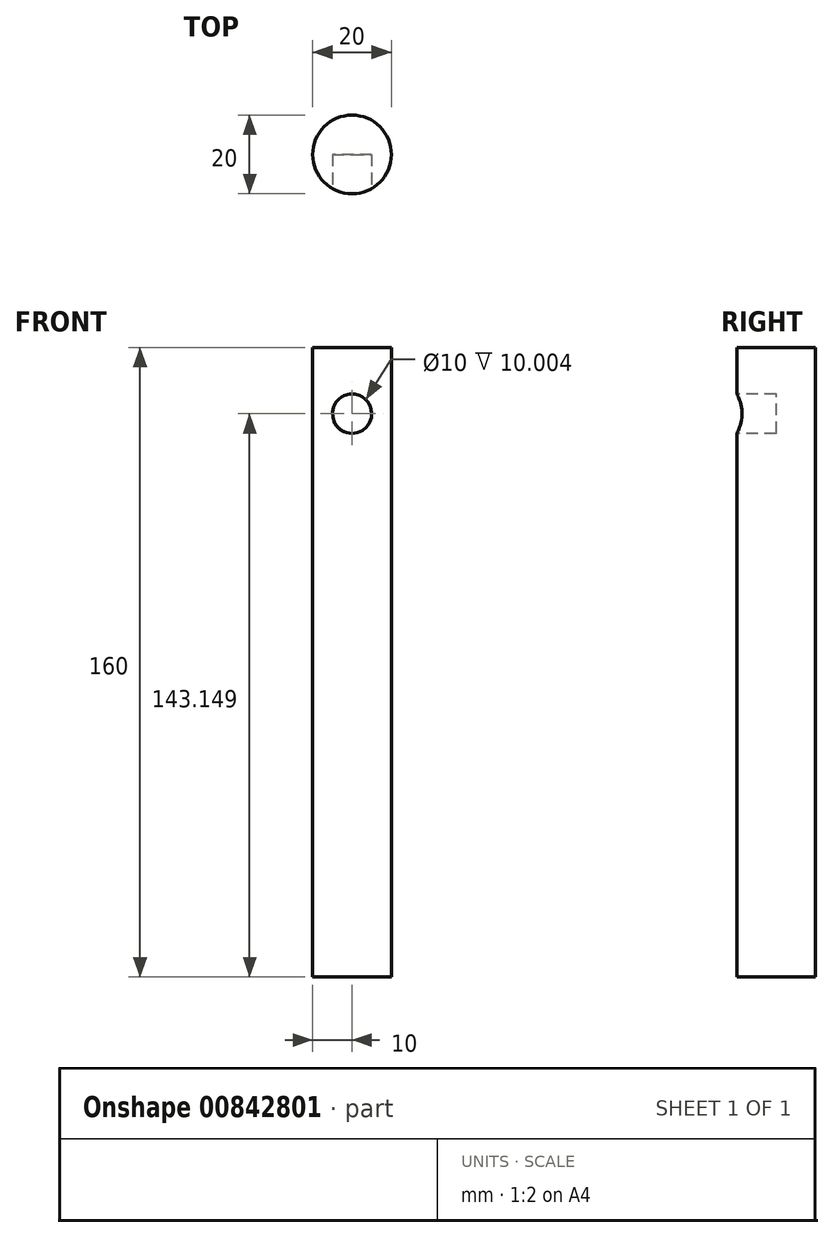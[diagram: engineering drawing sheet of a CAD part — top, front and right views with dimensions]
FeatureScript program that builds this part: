
annotation { "Feature Type Name" : "Feature", "Feature Type Description" : "" }
export const myFeature = defineFeature(function(context is Context, id is Id, definition is map)
    precondition{}
    {
        {
            var Q0;
            Q0=qCreatedBy(makeId("Top.planeOp"),FACE);
            var sketch = newSketch(context, id + "F0", { "sketchPlane" : qUnion([Q0])});
            skCircle(sketch, "E0", {"center": v(0, 0) * mm, "radius": 10 * mm});
            skSolve(sketch);
        }
        {
            var Q0;
            Q0=makeQuery(id+"F0.imprint","IMPRINT",FACE,{"disambiguationData":[TD([[makeQuery(id+"F0.imprint","IMPRINT",EDGE,{"derivedFrom":sQuery(id+"F0.wireOp",EDGE,"E0")}),1.0]])]});
            extrude(context, id + "F1", {"entities" : qUnion([Q0]), "oppositeDirection" : true, "depth" : 160 * mm, "offsetDistance" : 25 * mm});
        }
        {
            var Q0;
            Q0=qCreatedBy(makeId("Front.planeOp"),FACE);
            cPlane(context, id + "F2", {"entities" : qUnion([Q0]), "cplaneType" : CPlaneType.OFFSET, "offset" : 15 * mm, "width" : 150 * mm, "height" : 150 * mm});
        }
        {
            var Q0;
            Q0=qCreatedBy(id+"F2.planeOp",FACE);
            var sketch = newSketch(context, id + "F3", { "sketchPlane" : qUnion([Q0])});
            skCircle(sketch, "E1", {"center": v(0, -16.85) * mm, "radius": 5 * mm});
            skSolve(sketch);
        }
        {
            var Q0;
            Q0=makeQuery(id+"F3.imprint","IMPRINT",FACE,{"disambiguationData":[TD([[makeQuery(id+"F3.imprint","IMPRINT",EDGE,{"derivedFrom":sQuery(id+"F3.wireOp",EDGE,"E1")}),1.0]])]});
            var Q1;
            Q1=sQuery(id+"F3.wireOp",EDGE,"E1");
            extrude(context, id + "F4", {"entities" : qUnion([Q0]), "operationType" : NewBodyOperationType.REMOVE, "surfaceEntities" : qUnion([Q1]), "oppositeDirection" : true, "depth" : 15 * mm, "offsetDistance" : 25 * mm});
        }
    });
